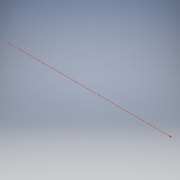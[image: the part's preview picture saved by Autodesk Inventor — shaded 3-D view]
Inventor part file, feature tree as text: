
AUTODESK INVENTOR PART (.ipt)
format: ipt  version: 2016 (Build 200138000, 138)  size: 91,648 bytes
history: native  units: mm
features: sketch x2, extrude x1, revolve x1
ambient origin geometry x8: Origin, YZ Plane, XZ Plane, XY Plane, X Axis, Y Axis, Z Axis, Center Point
bodies: Solid1 (feature_tree)
feature tree (4):
  extrude  "Extrusion1"  Depth=3000.0mm TaperAngle=0.0deg
  revolve  "Revolution1"  Angle=90.0deg
  sketch  "Sketch1"  dims[d0=5.0mm d1=3000.0mm d2=0.0mm]
  sketch  "Sketch2"  dims[d3=25.0mm d4=90.0deg]
